# Revit family: ledpanels-b4_re295-23_34w-840-u19_542016014600_0dd9
name_source: partatom
category: Lighting Fixtures
units: mm (PartAtom-declared; Revit-internal decimal feet)

## family parameters
Cut with Voids When Loaded = No
Host = Face
Light Source = No
Part Type = Normal
Room Calculation Point = No
Round Connector Dimension = Use Diameter
Shared = No

## types (1)
- LEDPanelS-B4 Re295-23/34W-840-U19 (1 x LED, 2990 lm, 4000)
    Apparent Load = 34 VA
    Approval mark = CE, ENEC
    CIE Flux Codes = 61 88 97 100 100
    Color Rendering = 80
    Color Temperature = 4000
    Control Gear = Electronic ballast
    Default Elevation = 1800 mm
    Description = Slim Panel Basic G4 Re295-23|27|31|34W-2990|3510|4030|4420lm-4000K-IP40-UGR19
    Frequency = 60 Hz
    Height = 0 mm  [stored 0 ft]
    Lamp = 1 x LED
    Lamp Light Flux = 2990 lm
    Lamp count = 1
    Length = 1195 mm
    Luminous efficacy = 88 lm/W
    Manufacturer = OPPLE
    ModVariant = No
    Model = 542016014600
    Mounting Place = Ceiling
    Mounting Type = Recessed
    Number of Poles = 1
    OnlyDefault = Yes
    Power Factor = 1
    Product Name = LEDPanelS-B4 Re295-23/34W-840-U19
    Product group = Spot Chiara
    ProductGroupID = 430
    Protection Class = Protection class II
    Protection Degree = IP 40
    RLX_Detail_Level = 1
    RLX_Emergency_Light_Flux = 0 lm
    RLX_Emergency_Type = 0
    RLX_Emergency_Type_DB = No
    RlxData = <blob elided: 162697 chars, md5=a777d0b7>
    Socket = socket
    Standby Power = 0 W
    System Light Flux = 2990 lm
    System Power = 34 W
    Type Comments = LED E C module 12W 2700K Clio CT
    Type Image = web_slimp_b4_re.jpg
    URL = http://relux.com
    VarID = ---
    Voltage = 230 V
    Voltage Range = 220-240 V
    Weight = 0.00 kg
    Width = 295 mm

note: [stored X ft] marks values corroborated as IEEE doubles in the binary element streams (Revit-internal decimal feet)

## geometry (parser evidence)
native form markers: Blend x4, Sweep x11
no freeform markers — native parametric forms only
